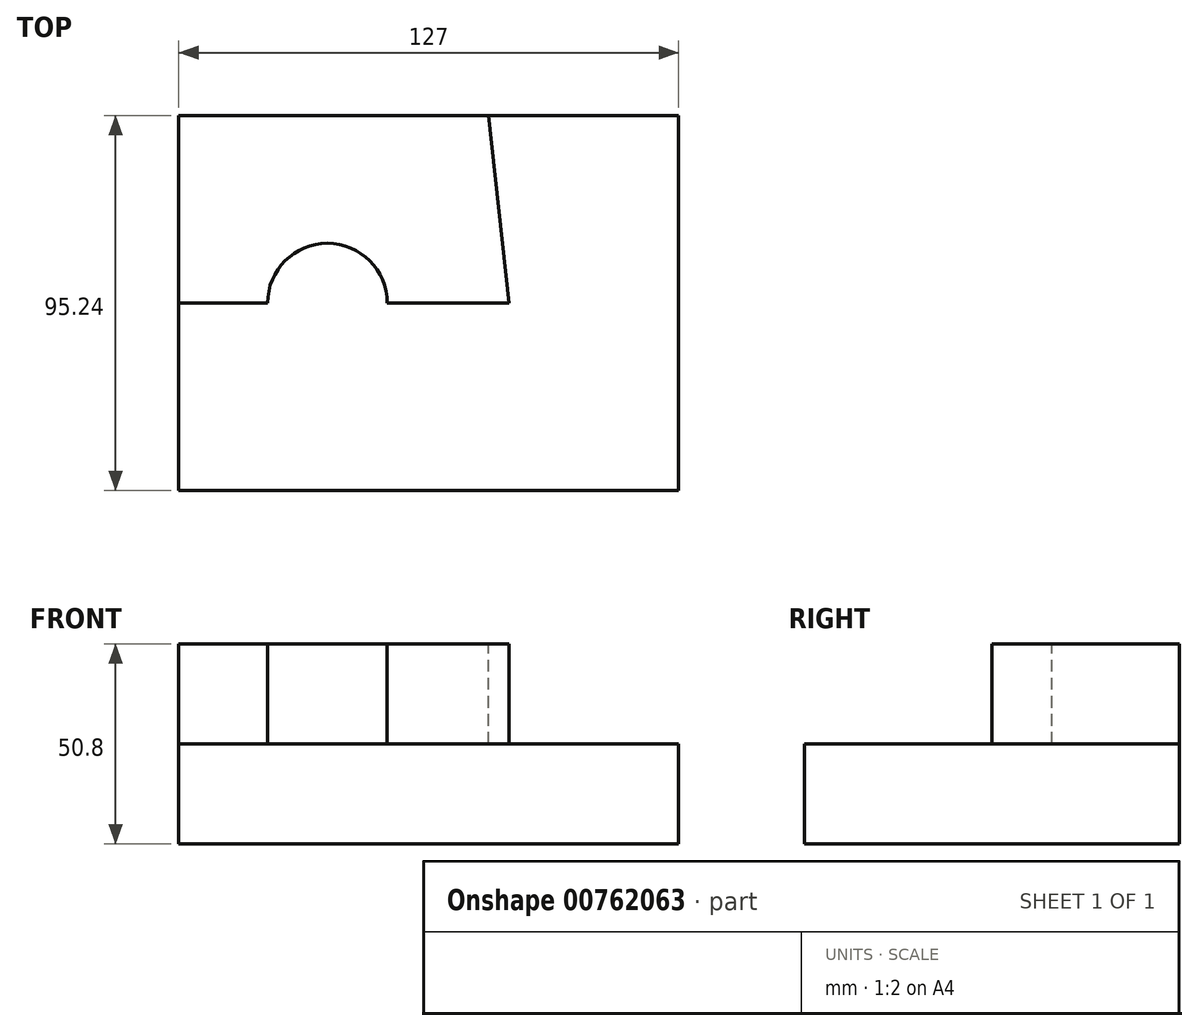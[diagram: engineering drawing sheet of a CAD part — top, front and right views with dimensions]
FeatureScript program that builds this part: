
annotation { "Feature Type Name" : "Feature", "Feature Type Description" : "" }
export const myFeature = defineFeature(function(context is Context, id is Id, definition is map)
    precondition{}
    {
        {
            var Q0;
            Q0=qCreatedBy(makeId("Top.planeOp"),FACE);
            var sketch = newSketch(context, id + "F0", { "sketchPlane" : qUnion([Q0])});
            skLineSegment(sketch, "E0.bottom", {"start": v(-63.5, 47.62) * mm, "end": v(63.5, 47.62) * mm});
            skLineSegment(sketch, "E0.top", {"start": v(-63.5, -47.62) * mm, "end": v(63.5, -47.62) * mm});
            skLineSegment(sketch, "E0.left", {"start": v(-63.5, 47.62) * mm, "end": v(-63.5, -47.62) * mm});
            skLineSegment(sketch, "E0.right", {"start": v(63.5, 47.62) * mm, "end": v(63.5, -47.62) * mm});
            skPoint(sketch, "E0.middle", {"position": v(0, 0) * mm});
            skSolve(sketch);
        }
        {
            var Q0;
            Q0 = qSketchRegion(id + "F0", true);
            extrude(context, id + "F1", {"entities" : qUnion([Q0]), "depth" : 25.4 * mm, "offsetDistance" : 25.4 * mm});
        }
        {
            var Q0;
            Q0=makeQuery(id+"F1.opExtrude","CAP_FACE",FACE,{"disambiguationData":[OSD([sQuery(id+"F0.wireOp",EDGE,"E0.bottom"),sQuery(id+"F0.wireOp",EDGE,"E0.top"),sQuery(id+"F0.wireOp",EDGE,"E0.left"),sQuery(id+"F0.wireOp",EDGE,"E0.right")])],"isStart":false});
            var sketch = newSketch(context, id + "F2", { "sketchPlane" : qUnion([Q0])});
            skLineSegment(sketch, "E1", {"start": v(-63.5, 0) * mm, "end": v(63.5, 0) * mm});
            skSolve(sketch);
        }
        {
            var Q0;
            {var subQ0=sQuery(id+"F2.wireOp",EDGE,"E1");Q0=makeQuery(id+"F2.imprint","IMPRINT",FACE,{"disambiguationData":[TD([[makeQuery(id+"F2.imprint","IMPRINT",EDGE,{"derivedFrom":subQ0}),1.0]])]});}
            extrude(context, id + "F3", {"entities" : qUnion([Q0]), "operationType" : NewBodyOperationType.ADD, "depth" : 25.4 * mm, "offsetDistance" : 25.4 * mm});
        }
        {
            var Q0;
            Q0=makeQuery(id+"F3.opExtrude","CAP_FACE",FACE,{"disambiguationData":[OSD([sQuery(id+"F0.wireOp",EDGE,"E0.bottom"),sQuery(id+"F0.wireOp",EDGE,"E0.left"),sQuery(id+"F0.wireOp",EDGE,"E0.right"),sQuery(id+"F2.wireOp",EDGE,"E1")])],"isStart":false});
            var sketch = newSketch(context, id + "F4", { "sketchPlane" : qUnion([Q0])});
            skLineSegment(sketch, "E2", {"start": v(15.25, 47.62) * mm, "end": v(20.44, 0) * mm});
            skCircle(sketch, "E3", {"center": v(-25.73, 0) * mm, "radius": 15.18 * mm});
            skSolve(sketch);
        }
        {
            var Q0;
            {var subQ0=sQuery(id+"F4.wireOp",EDGE,"E3");var subQ1=makeQuery(id+"F3.opExtrude","CAP_EDGE",EDGE,{"disambiguationData":[OSD([sQuery(id+"F2.wireOp",EDGE,"E1")])],"isStart":false});var subQ2=makeQuery(id+"F4.imprint","INTERSECT",VERTEX,{"disambiguationData":[OD(0.0)],"derivedFrom":[subQ1,subQ0]});Q0=makeQuery(id+"F4.imprint","IMPRINT",FACE,{"disambiguationData":[TD([[makeQuery(id+"F4.imprint","IMPRINT",EDGE,{"disambiguationData":[TD([[subQ2,1.0]])],"derivedFrom":subQ0}),1.0]])]});}
            var Q1;
            {var subQ0=sQuery(id+"F4.wireOp",EDGE,"E2");Q1=makeQuery(id+"F4.imprint","IMPRINT",FACE,{"disambiguationData":[TD([[makeQuery(id+"F4.imprint","IMPRINT",EDGE,{"derivedFrom":subQ0}),1.0]])]});}
            extrude(context, id + "F5", {"entities" : qUnion([Q0, Q1]), "operationType" : NewBodyOperationType.REMOVE, "oppositeDirection" : true, "depth" : 25.4 * mm, "offsetDistance" : 25.4 * mm});
        }
    });
